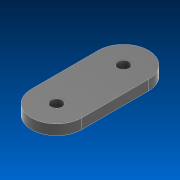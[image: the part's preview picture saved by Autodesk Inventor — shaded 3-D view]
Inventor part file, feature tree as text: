
AUTODESK INVENTOR PART (.ipt)
format: ipt  version: 2022.2 (Build 262287000, 287)  size: 92,672 bytes
history: native  units: in
note: dims shown in document units (in); Inventor stores cm internally (conversion verified against a paired STEP export)
features: extrude x1, sketch x1
ambient origin geometry x8: Origin, YZ Plane, XZ Plane, XY Plane, X Axis, Y Axis, Z Axis, Center Point
bodies: Solid1 (feature_tree)
feature tree (2):
  extrude  "Extrusion1"  Depth=1.0in
  sketch  "Sketch1"  dims[d0=0.17in d2=1.0in d3=0.75in d4=0.152in d5=0.0in]
